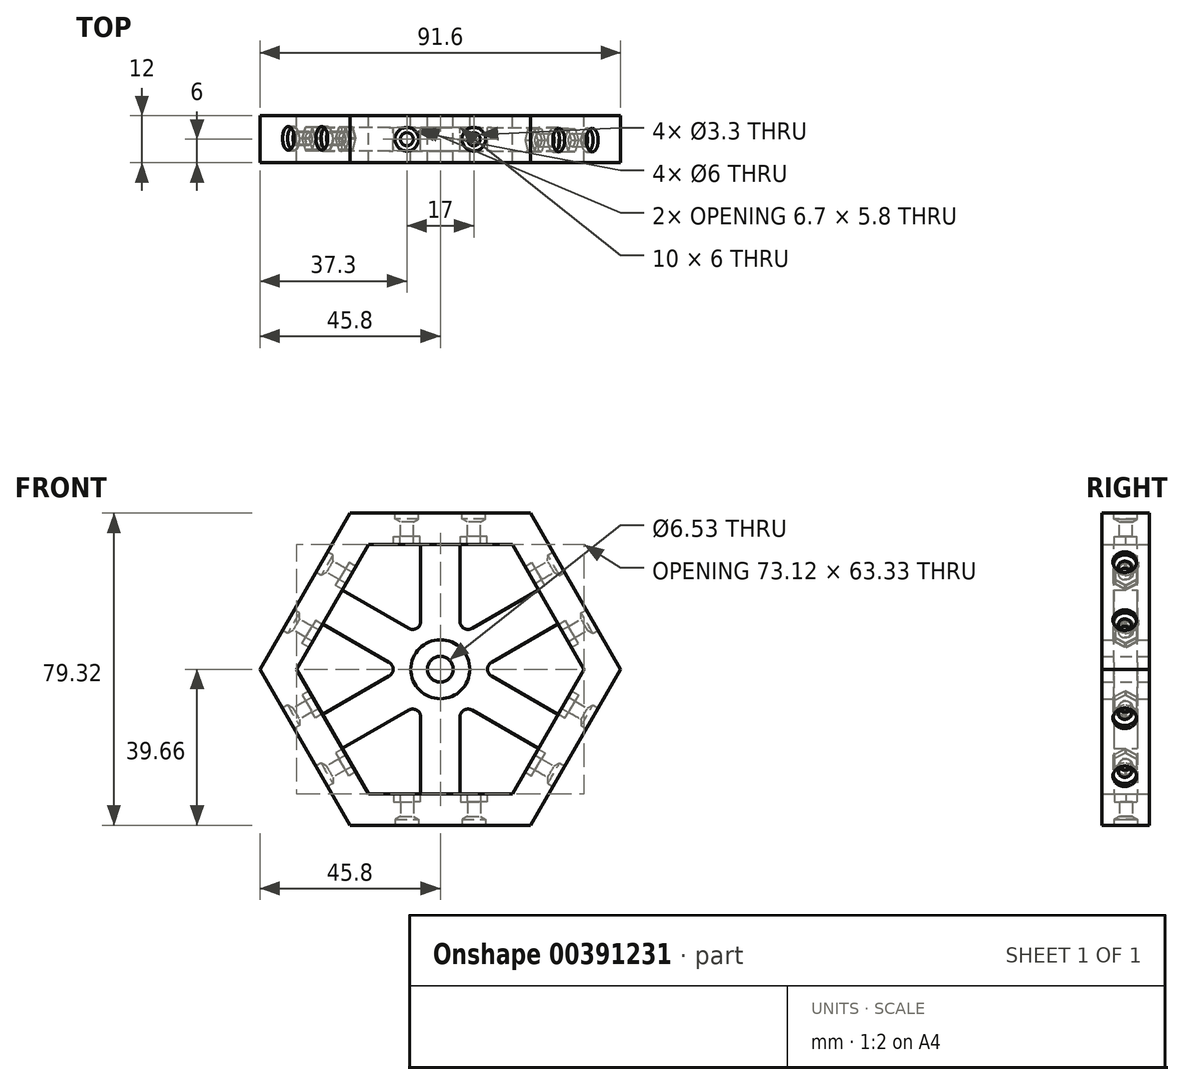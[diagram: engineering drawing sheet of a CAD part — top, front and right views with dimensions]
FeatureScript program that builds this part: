
annotation { "Feature Type Name" : "Feature", "Feature Type Description" : "" }
export const myFeature = defineFeature(function(context is Context, id is Id, definition is map)
    precondition{}
    {
        {
            var Q0;
            Q0=qCreatedBy(makeId("Front.planeOp"),FACE);
            var sketch = newSketch(context, id + "F0", { "sketchPlane" : qUnion([Q0])});
            skCircle(sketch, "E0.cCircle", {"center": v(0, 0) * mm, "radius": 39.66 * mm, "construction": true});
            skLineSegment(sketch, "E0.0", {"start": v(45.8, 0) * mm, "end": v(22.9, -39.66) * mm});
            skLineSegment(sketch, "E0.1", {"start": v(22.9, -39.66) * mm, "end": v(-22.9, -39.66) * mm});
            skLineSegment(sketch, "E0.2", {"start": v(-22.9, -39.66) * mm, "end": v(-45.8, 0) * mm});
            skLineSegment(sketch, "E0.3", {"start": v(-45.8, 0) * mm, "end": v(-22.9, 39.66) * mm});
            skLineSegment(sketch, "E0.4", {"start": v(-22.9, 39.66) * mm, "end": v(22.9, 39.66) * mm});
            skLineSegment(sketch, "E0.5", {"start": v(22.9, 39.66) * mm, "end": v(45.8, 0) * mm});
            skPoint(sketch, "E0.0.midPoint", {"position": v(34.35, -19.83) * mm});
            skCircle(sketch, "E1.cCircle", {"center": v(0, 0) * mm, "radius": 31.66 * mm, "construction": true});
            skLineSegment(sketch, "E1.0", {"start": v(36.56, 0) * mm, "end": v(18.28, -31.66) * mm});
            skLineSegment(sketch, "E1.1", {"start": v(18.28, -31.66) * mm, "end": v(-18.28, -31.66) * mm});
            skLineSegment(sketch, "E1.2", {"start": v(-18.28, -31.66) * mm, "end": v(-36.56, 0) * mm});
            skLineSegment(sketch, "E1.3", {"start": v(-36.56, 0) * mm, "end": v(-18.28, 31.66) * mm});
            skLineSegment(sketch, "E1.4", {"start": v(-18.28, 31.66) * mm, "end": v(18.28, 31.66) * mm});
            skLineSegment(sketch, "E1.5", {"start": v(18.28, 31.66) * mm, "end": v(36.56, 0) * mm});
            skPoint(sketch, "E1.0.midPoint", {"position": v(27.42, -15.83) * mm});
            skCircle(sketch, "E2", {"center": v(0, 0) * mm, "radius": 5 * mm});
            skLineSegment(sketch, "E3", {"start": v(5, -12.12) * mm, "end": v(5, -31.66) * mm});
            skLineSegment(sketch, "E4", {"start": v(-5, -12.12) * mm, "end": v(-5, -31.66) * mm});
            skLineSegment(sketch, "E5", {"start": v(-8, 10.4) * mm, "end": v(-24.92, 20.16) * mm});
            skLineSegment(sketch, "E6", {"start": v(-5, 12.12) * mm, "end": v(-5, 31.66) * mm});
            skLineSegment(sketch, "E7", {"start": v(5, 12.12) * mm, "end": v(5, 31.66) * mm});
            skLineSegment(sketch, "E8", {"start": v(-13, -1.73) * mm, "end": v(-29.92, -11.5) * mm});
            skLineSegment(sketch, "E9", {"start": v(-8, -10.4) * mm, "end": v(-24.92, -20.16) * mm});
            skLineSegment(sketch, "E10", {"start": v(8, -10.4) * mm, "end": v(24.92, -20.16) * mm});
            skLineSegment(sketch, "E11", {"start": v(13, -1.73) * mm, "end": v(29.92, -11.5) * mm});
            skLineSegment(sketch, "E12", {"start": v(13, 1.73) * mm, "end": v(29.92, 11.5) * mm});
            skLineSegment(sketch, "E13", {"start": v(8, 10.4) * mm, "end": v(24.92, 20.16) * mm});
            skLineSegment(sketch, "E14", {"start": v(-13, 1.73) * mm, "end": v(-29.92, 11.5) * mm});
            skArc(sketch, "E15.filletArc", {"start": v(13, 1.73) * mm, "mid": v(12, 0) * mm, "end": v(13, -1.73) * mm});
            skArc(sketch, "E16.filletArc", {"start": v(5, 12.12) * mm, "mid": v(6, 10.4) * mm, "end": v(8, 10.4) * mm});
            skArc(sketch, "E17.filletArc", {"start": v(-8, 10.4) * mm, "mid": v(-6, 10.4) * mm, "end": v(-5, 12.12) * mm});
            skArc(sketch, "E18.filletArc", {"start": v(-13, -1.73) * mm, "mid": v(-12, 0) * mm, "end": v(-13, 1.73) * mm});
            skPoint(sketch, "E19.newPointB", {"position": v(-5, 0) * mm});
            skArc(sketch, "E19.filletArc", {"start": v(-5, -12.12) * mm, "mid": v(-6, -10.4) * mm, "end": v(-8, -10.4) * mm});
            skPoint(sketch, "E20.newPointA", {"position": v(5, 0) * mm});
            skArc(sketch, "E20.filletArc", {"start": v(8, -10.4) * mm, "mid": v(6, -10.4) * mm, "end": v(5, -12.12) * mm});
            skCircle(sketch, "E21", {"center": v(0, 0) * mm, "radius": 7.5 * mm});
            skSolve(sketch);
        }
        {
            var Q0;
            Q0=makeQuery(id+"F0.imprint","IMPRINT",FACE,{"disambiguationData":[TD([[makeQuery(id+"F0.imprint","IMPRINT",EDGE,{"derivedFrom":sQuery(id+"F0.wireOp",EDGE,"E0.0")}),-1.0]])]});
            extrude(context, id + "F1", {"entities" : qUnion([Q0]), "depth" : 12 * mm});
        }
        {
            var Q0;
            {var subQ0=sQuery(id+"F0.wireOp",EDGE,"E6");var subQ1=sQuery(id+"F0.wireOp",EDGE,"E1.4");var subQ2=makeQuery(id+"F0.imprint","INTERSECT",VERTEX,{"derivedFrom":[subQ1,subQ0]});Q0=makeQuery(id+"F0.imprint","IMPRINT",FACE,{"disambiguationData":[TD([[makeQuery(id+"F0.imprint","IMPRINT",EDGE,{"disambiguationData":[TD([[subQ2,-1.0]])],"derivedFrom":subQ1}),-1.0]])]});}
            var Q1;
            {var subQ5=sQuery(id+"F0.wireOp",EDGE,"E3");var subQ6=sQuery(id+"F0.wireOp",EDGE,"E1.1");var subQ7=makeQuery(id+"F0.imprint","INTERSECT",VERTEX,{"derivedFrom":[subQ6,subQ5]});Q1=makeQuery(id+"F0.imprint","IMPRINT",FACE,{"disambiguationData":[TD([[makeQuery(id+"F0.imprint","IMPRINT",EDGE,{"disambiguationData":[TD([[subQ7,-1.0]])],"derivedFrom":subQ6}),-1.0]])]});}
            var Q2;
            {var subQ1=sQuery(id+"F0.wireOp",EDGE,"E1.2");var subQ5=sQuery(id+"F0.wireOp",EDGE,"E8");var subQ6=makeQuery(id+"F0.imprint","INTERSECT",VERTEX,{"derivedFrom":[subQ1,subQ5]});Q2=makeQuery(id+"F0.imprint","IMPRINT",FACE,{"disambiguationData":[TD([[makeQuery(id+"F0.imprint","IMPRINT",EDGE,{"disambiguationData":[TD([[subQ6,1.0]])],"derivedFrom":subQ1}),-1.0]])]});}
            var Q3;
            {var subQ1=sQuery(id+"F0.wireOp",EDGE,"E5");var subQ5=sQuery(id+"F0.wireOp",EDGE,"E1.3");var subQ6=makeQuery(id+"F0.imprint","INTERSECT",VERTEX,{"derivedFrom":[subQ5,subQ1]});Q3=makeQuery(id+"F0.imprint","IMPRINT",FACE,{"disambiguationData":[TD([[makeQuery(id+"F0.imprint","IMPRINT",EDGE,{"disambiguationData":[TD([[subQ6,1.0]])],"derivedFrom":subQ5}),-1.0]])]});}
            var Q4;
            {var subQ0=sQuery(id+"F0.wireOp",EDGE,"E10");var subQ1=sQuery(id+"F0.wireOp",EDGE,"E1.0");var subQ2=makeQuery(id+"F0.imprint","INTERSECT",VERTEX,{"derivedFrom":[subQ1,subQ0]});Q4=makeQuery(id+"F0.imprint","IMPRINT",FACE,{"disambiguationData":[TD([[makeQuery(id+"F0.imprint","IMPRINT",EDGE,{"disambiguationData":[TD([[subQ2,1.0]])],"derivedFrom":subQ1}),-1.0]])]});}
            var Q5;
            {var subQ0=sQuery(id+"F0.wireOp",EDGE,"E12");var subQ1=sQuery(id+"F0.wireOp",EDGE,"E1.5");var subQ2=makeQuery(id+"F0.imprint","INTERSECT",VERTEX,{"derivedFrom":[subQ1,subQ0]});Q5=makeQuery(id+"F0.imprint","IMPRINT",FACE,{"disambiguationData":[TD([[makeQuery(id+"F0.imprint","IMPRINT",EDGE,{"disambiguationData":[TD([[subQ2,1.0]])],"derivedFrom":subQ1}),-1.0]])]});}
            var Q6;
            {var subQ0=sQuery(id+"F0.wireOp",EDGE,"E7");var subQ5=sQuery(id+"F0.wireOp",EDGE,"E11");var subQ6=makeQuery(id+"F0.imprint","INTERSECT",VERTEX,{"derivedFrom":[subQ0,subQ5]});Q6=makeQuery(id+"F0.imprint","IMPRINT",FACE,{"disambiguationData":[TD([[makeQuery(id+"F0.imprint","IMPRINT",EDGE,{"disambiguationData":[TD([[subQ6,-1.0]])],"derivedFrom":subQ5}),-1.0]])]});}
            var Q7;
            {var subQ0=sQuery(id+"F0.wireOp",EDGE,"E11");var subQ5=sQuery(id+"F0.wireOp",EDGE,"E7");var subQ7=makeQuery(id+"F0.imprint","INTERSECT",VERTEX,{"derivedFrom":[subQ5,subQ0]});Q7=makeQuery(id+"F0.imprint","IMPRINT",FACE,{"disambiguationData":[TD([[makeQuery(id+"F0.imprint","IMPRINT",EDGE,{"disambiguationData":[TD([[subQ7,-1.0]])],"derivedFrom":subQ5}),1.0]])]});}
            var Q8;
            {var subQ0=sQuery(id+"F0.wireOp",EDGE,"E13");var subQ1=sQuery(id+"F0.wireOp",EDGE,"E5");var subQ2=makeQuery(id+"F0.imprint","INTERSECT",VERTEX,{"derivedFrom":[subQ1,subQ0]});Q8=makeQuery(id+"F0.imprint","IMPRINT",FACE,{"disambiguationData":[TD([[makeQuery(id+"F0.imprint","IMPRINT",EDGE,{"disambiguationData":[TD([[subQ2,-1.0]])],"derivedFrom":subQ1}),1.0]])]});}
            var Q9;
            {var subQ0=sQuery(id+"F0.wireOp",EDGE,"E6");var subQ5=sQuery(id+"F0.wireOp",EDGE,"E8");var subQ6=makeQuery(id+"F0.imprint","INTERSECT",VERTEX,{"derivedFrom":[subQ0,subQ5]});Q9=makeQuery(id+"F0.imprint","IMPRINT",FACE,{"disambiguationData":[TD([[makeQuery(id+"F0.imprint","IMPRINT",EDGE,{"disambiguationData":[TD([[subQ6,-1.0]])],"derivedFrom":subQ5}),1.0]])]});}
            var Q10;
            {var subQ0=sQuery(id+"F0.wireOp",EDGE,"E14");var subQ1=sQuery(id+"F0.wireOp",EDGE,"E4");var subQ2=makeQuery(id+"F0.imprint","INTERSECT",VERTEX,{"derivedFrom":[subQ1,subQ0]});Q10=makeQuery(id+"F0.imprint","IMPRINT",FACE,{"disambiguationData":[TD([[makeQuery(id+"F0.imprint","IMPRINT",EDGE,{"disambiguationData":[TD([[subQ2,-1.0]])],"derivedFrom":subQ1}),1.0]])]});}
            var Q11;
            {var subQ0=sQuery(id+"F0.wireOp",EDGE,"E12");var subQ1=sQuery(id+"F0.wireOp",EDGE,"E3");var subQ2=makeQuery(id+"F0.imprint","INTERSECT",VERTEX,{"derivedFrom":[subQ1,subQ0]});Q11=makeQuery(id+"F0.imprint","IMPRINT",FACE,{"disambiguationData":[TD([[makeQuery(id+"F0.imprint","IMPRINT",EDGE,{"disambiguationData":[TD([[subQ2,-1.0]])],"derivedFrom":subQ1}),-1.0]])]});}
            var Q12;
            {var subQ0=sQuery(id+"F0.wireOp",EDGE,"E5");var subQ3=sQuery(id+"F0.wireOp",EDGE,"E13");var subQ5=makeQuery(id+"F0.imprint","INTERSECT",VERTEX,{"derivedFrom":[subQ0,subQ3]});Q12=makeQuery(id+"F0.imprint","IMPRINT",FACE,{"disambiguationData":[TD([[makeQuery(id+"F0.imprint","IMPRINT",EDGE,{"disambiguationData":[TD([[subQ5,1.0]])],"derivedFrom":subQ0}),1.0]])]});}
            var Q13;
            {var subQ0=sQuery(id+"F0.wireOp",EDGE,"E6");var subQ3=sQuery(id+"F0.wireOp",EDGE,"E8");var subQ5=makeQuery(id+"F0.imprint","INTERSECT",VERTEX,{"derivedFrom":[subQ0,subQ3]});Q13=makeQuery(id+"F0.imprint","IMPRINT",FACE,{"disambiguationData":[TD([[makeQuery(id+"F0.imprint","IMPRINT",EDGE,{"disambiguationData":[TD([[subQ5,1.0]])],"derivedFrom":subQ0}),-1.0]])]});}
            var Q14;
            {var subQ0=sQuery(id+"F0.wireOp",EDGE,"E4");var subQ3=sQuery(id+"F0.wireOp",EDGE,"E14");var subQ5=makeQuery(id+"F0.imprint","INTERSECT",VERTEX,{"derivedFrom":[subQ0,subQ3]});Q14=makeQuery(id+"F0.imprint","IMPRINT",FACE,{"disambiguationData":[TD([[makeQuery(id+"F0.imprint","IMPRINT",EDGE,{"disambiguationData":[TD([[subQ5,1.0]])],"derivedFrom":subQ0}),1.0]])]});}
            var Q15;
            {var subQ0=sQuery(id+"F0.wireOp",EDGE,"E9");var subQ3=sQuery(id+"F0.wireOp",EDGE,"E10");var subQ5=makeQuery(id+"F0.imprint","INTERSECT",VERTEX,{"derivedFrom":[subQ0,subQ3]});Q15=makeQuery(id+"F0.imprint","IMPRINT",FACE,{"disambiguationData":[TD([[makeQuery(id+"F0.imprint","IMPRINT",EDGE,{"disambiguationData":[TD([[subQ5,1.0]])],"derivedFrom":subQ0}),-1.0]])]});}
            var Q16;
            {var subQ0=sQuery(id+"F0.wireOp",EDGE,"E3");var subQ3=sQuery(id+"F0.wireOp",EDGE,"E12");var subQ5=makeQuery(id+"F0.imprint","INTERSECT",VERTEX,{"derivedFrom":[subQ0,subQ3]});Q16=makeQuery(id+"F0.imprint","IMPRINT",FACE,{"disambiguationData":[TD([[makeQuery(id+"F0.imprint","IMPRINT",EDGE,{"disambiguationData":[TD([[subQ5,1.0]])],"derivedFrom":subQ0}),-1.0]])]});}
            var Q17;
            {var subQ0=sQuery(id+"F0.wireOp",EDGE,"E7");var subQ3=sQuery(id+"F0.wireOp",EDGE,"E11");var subQ5=makeQuery(id+"F0.imprint","INTERSECT",VERTEX,{"derivedFrom":[subQ0,subQ3]});Q17=makeQuery(id+"F0.imprint","IMPRINT",FACE,{"disambiguationData":[TD([[makeQuery(id+"F0.imprint","IMPRINT",EDGE,{"disambiguationData":[TD([[subQ5,1.0]])],"derivedFrom":subQ0}),1.0]])]});}
            var Q18;
            Q18=makeQuery(id+"F0.imprint","IMPRINT",FACE,{"disambiguationData":[TD([[makeQuery(id+"F0.imprint","IMPRINT",EDGE,{"derivedFrom":sQuery(id+"F0.wireOp",EDGE,"E2")}),1.0]])]});
            var Q19;
            Q19=makeQuery(id+"F0.imprint","IMPRINT",FACE,{"disambiguationData":[TD([[makeQuery(id+"F0.imprint","IMPRINT",EDGE,{"derivedFrom":sQuery(id+"F0.wireOp",EDGE,"E2")}),-1.0]])]});
            extrude(context, id + "F2", {"entities" : qUnion([Q0, Q1, Q2, Q3, Q4, Q5, Q6, Q7, Q8, Q9, Q10, Q11, Q12, Q13, Q14, Q15, Q16, Q17, Q18, Q19]), "operationType" : NewBodyOperationType.ADD, "depth" : 9 * mm, "hasSecondDirection" : true, "secondDirectionOppositeDirection" : false, "secondDirectionDepth" : 3 * mm});
        }
        {
            var Q0;
            Q0=makeQuery(id+"F1.opExtrude","SWEPT_FACE",FACE,{"disambiguationData":[OSD([sQuery(id+"F0.wireOp",EDGE,"E0.2")])]});
            var sketch = newSketch(context, id + "F3", { "sketchPlane" : qUnion([Q0])});
            skPoint(sketch, "E22", {"position": v(6, -8.5) * mm});
            skPoint(sketch, "E22.positionSnap0", {"position": v(6, -22.9) * mm});
            skPoint(sketch, "E23", {"position": v(6, 8.5) * mm});
            skCircle(sketch, "E24.cCircle", {"center": v(6, -8.5) * mm, "radius": 2.9 * mm, "construction": true});
            skLineSegment(sketch, "E24.0", {"start": v(6, -5.15) * mm, "end": v(8.9, -6.83) * mm});
            skLineSegment(sketch, "E24.1", {"start": v(8.9, -6.83) * mm, "end": v(8.9, -10.17) * mm});
            skLineSegment(sketch, "E24.2", {"start": v(8.9, -10.17) * mm, "end": v(6, -11.85) * mm});
            skLineSegment(sketch, "E24.3", {"start": v(6, -11.85) * mm, "end": v(3.1, -10.17) * mm});
            skLineSegment(sketch, "E24.4", {"start": v(3.1, -10.17) * mm, "end": v(3.1, -6.83) * mm});
            skLineSegment(sketch, "E24.5", {"start": v(3.1, -6.83) * mm, "end": v(6, -5.15) * mm});
            skPoint(sketch, "E24.0.midPoint", {"position": v(7.45, -5.99) * mm});
            skCircle(sketch, "E25.cCircle", {"center": v(6, 8.5) * mm, "radius": 2.9 * mm, "construction": true});
            skLineSegment(sketch, "E25.0", {"start": v(8.9, 10.17) * mm, "end": v(8.9, 6.83) * mm});
            skLineSegment(sketch, "E25.1", {"start": v(8.9, 6.83) * mm, "end": v(6, 5.15) * mm});
            skLineSegment(sketch, "E25.2", {"start": v(6, 5.15) * mm, "end": v(3.1, 6.83) * mm});
            skLineSegment(sketch, "E25.3", {"start": v(3.1, 6.83) * mm, "end": v(3.1, 10.17) * mm});
            skLineSegment(sketch, "E25.4", {"start": v(3.1, 10.17) * mm, "end": v(6, 11.85) * mm});
            skLineSegment(sketch, "E25.5", {"start": v(6, 11.85) * mm, "end": v(8.9, 10.17) * mm});
            skPoint(sketch, "E25.0.midPoint", {"position": v(8.9, 8.5) * mm});
            skSolve(sketch);
        }
        {
            var Q0;
            Q0=qSketchRegion(id+"F3",true);
            extrude(context, id + "F4", {"entities" : qUnion([Q0]), "operationType" : NewBodyOperationType.REMOVE, "oppositeDirection" : true, "depth" : 9 * mm, "hasSecondDirection" : true, "secondDirectionOppositeDirection" : true, "secondDirectionDepth" : 6 * mm});
        }
        {
            var Q0;
            Q0=sQuery(id+"F3.wireOp",VERTEX,"E22");
            var Q1;
            Q1=sQuery(id+"F3.wireOp",VERTEX,"E23");
            var Q2;
            Q2=makeQuery(id+"F1.opExtrude","SWEPT_BODY",BODY,{"disambiguationData":[OSD([sQuery(id+"F0.wireOp",EDGE,"E0.0"),sQuery(id+"F0.wireOp",EDGE,"E0.1"),sQuery(id+"F0.wireOp",EDGE,"E0.2"),sQuery(id+"F0.wireOp",EDGE,"E0.3"),sQuery(id+"F0.wireOp",EDGE,"E0.4"),sQuery(id+"F0.wireOp",EDGE,"E0.5"),sQuery(id+"F0.wireOp",EDGE,"E1.0"),sQuery(id+"F0.wireOp",EDGE,"E1.1"),sQuery(id+"F0.wireOp",EDGE,"E1.2"),sQuery(id+"F0.wireOp",EDGE,"E1.3"),sQuery(id+"F0.wireOp",EDGE,"E1.4"),sQuery(id+"F0.wireOp",EDGE,"E1.5")])]});
            hole(context, id + "F5", {"style" : HoleStyle.SIMPLE, "endStyle" : HoleEndStyle.BLIND, "standardTappedOrClearance" : lookupTablePath({ "standard" : "ISO", "fit" : "Normal", "size" : "M3", "type" : "Clearance" }), "standardBlindInLast" : lookupTablePath({ "fit" : "Standard", "standard" : "ISO", "size" : "M3", "type" : "Clearance" }), "holeDiameter" : 3.3 * mm, "holeDepth" : 13.5 * mm, "tappedDepth" : 12 * mm, "tapClearance" : 3, "locations" : qUnion([Q0, Q1]), "scope" : qUnion([Q2])});
        }
        {
            var Q0;
            Q0=sQuery(id+"F3.wireOp",VERTEX,"E22");
            var Q1;
            Q1=sQuery(id+"F3.wireOp",VERTEX,"E23");
            var Q2;
            Q2=makeQuery(id+"F1.opExtrude","SWEPT_BODY",BODY,{"disambiguationData":[OSD([sQuery(id+"F0.wireOp",EDGE,"E0.0"),sQuery(id+"F0.wireOp",EDGE,"E0.1"),sQuery(id+"F0.wireOp",EDGE,"E0.2"),sQuery(id+"F0.wireOp",EDGE,"E0.3"),sQuery(id+"F0.wireOp",EDGE,"E0.4"),sQuery(id+"F0.wireOp",EDGE,"E0.5"),sQuery(id+"F0.wireOp",EDGE,"E1.0"),sQuery(id+"F0.wireOp",EDGE,"E1.1"),sQuery(id+"F0.wireOp",EDGE,"E1.2"),sQuery(id+"F0.wireOp",EDGE,"E1.3"),sQuery(id+"F0.wireOp",EDGE,"E1.4"),sQuery(id+"F0.wireOp",EDGE,"E1.5")])]});
            hole(context, id + "F6", {"style" : HoleStyle.SIMPLE, "endStyle" : HoleEndStyle.BLIND, "holeDiameter" : 6 * mm, "holeDepth" : 1.5 * mm, "tappedDepth" : 12 * mm, "tapClearance" : 3, "locations" : qUnion([Q0, Q1]), "scope" : qUnion([Q2])});
        }
        {
            var Q0;
            Q0=makeQuery(id+"F0.imprint","IMPRINT",FACE,{"disambiguationData":[TD([[makeQuery(id+"F0.imprint","IMPRINT",EDGE,{"derivedFrom":sQuery(id+"F0.wireOp",EDGE,"E2")}),-1.0]])]});
            var Q1;
            Q1=makeQuery(id+"F0.imprint","IMPRINT",FACE,{"disambiguationData":[TD([[makeQuery(id+"F0.imprint","IMPRINT",EDGE,{"derivedFrom":sQuery(id+"F0.wireOp",EDGE,"E2")}),1.0]])]});
            extrude(context, id + "F7", {"entities" : qUnion([Q0, Q1]), "operationType" : NewBodyOperationType.ADD, "depth" : 12 * mm});
        }
        {
            var Q0;
            Q0=sQuery(id+"F0.wireOp",VERTEX,"E21.center");
            var Q1;
            Q1=makeQuery(id+"F1.opExtrude","SWEPT_BODY",BODY,{"disambiguationData":[OSD([sQuery(id+"F0.wireOp",EDGE,"E0.0"),sQuery(id+"F0.wireOp",EDGE,"E0.1"),sQuery(id+"F0.wireOp",EDGE,"E0.2"),sQuery(id+"F0.wireOp",EDGE,"E0.3"),sQuery(id+"F0.wireOp",EDGE,"E0.4"),sQuery(id+"F0.wireOp",EDGE,"E0.5"),sQuery(id+"F0.wireOp",EDGE,"E1.0"),sQuery(id+"F0.wireOp",EDGE,"E1.1"),sQuery(id+"F0.wireOp",EDGE,"E1.2"),sQuery(id+"F0.wireOp",EDGE,"E1.3"),sQuery(id+"F0.wireOp",EDGE,"E1.4"),sQuery(id+"F0.wireOp",EDGE,"E1.5")])]});
            hole(context, id + "F8", {"style" : HoleStyle.SIMPLE, "endStyle" : HoleEndStyle.BLIND, "oppositeDirection" : true, "standardTappedOrClearance" : lookupTablePath({ "standard" : "ANSI", "fit" : "Close", "size" : "1/4", "type" : "Clearance" }), "standardBlindInLast" : lookupTablePath({ "fit" : "Close", "standard" : "ANSI", "size" : "1/4", "type" : "Clearance" }), "holeDiameter" : 6.53 * mm, "holeDepth" : 15.8 * mm, "tappedDepth" : 12 * mm, "tapClearance" : 3, "locations" : qUnion([Q0]), "scope" : qUnion([Q1])});
        }
        {
            var Q0;
            Q0=makeQuery(id+"F1.opExtrude","SWEPT_FACE",FACE,{"disambiguationData":[OSD([sQuery(id+"F0.wireOp",EDGE,"E0.3")])]});
            var sketch = newSketch(context, id + "F9", { "sketchPlane" : qUnion([Q0])});
            skPoint(sketch, "E26", {"position": v(5.77, -8.5) * mm});
            skPoint(sketch, "E26.positionSnap0", {"position": v(5.77, -22.9) * mm});
            skPoint(sketch, "E27", {"position": v(5.77, 8.5) * mm});
            skCircle(sketch, "E28.cCircle", {"center": v(5.77, -8.5) * mm, "radius": 2.9 * mm, "construction": true});
            skLineSegment(sketch, "E28.0", {"start": v(5.77, -5.15) * mm, "end": v(8.67, -6.83) * mm});
            skLineSegment(sketch, "E28.1", {"start": v(8.67, -6.83) * mm, "end": v(8.67, -10.17) * mm});
            skLineSegment(sketch, "E28.2", {"start": v(8.67, -10.17) * mm, "end": v(5.77, -11.85) * mm});
            skLineSegment(sketch, "E28.3", {"start": v(5.77, -11.85) * mm, "end": v(2.87, -10.17) * mm});
            skLineSegment(sketch, "E28.4", {"start": v(2.87, -10.17) * mm, "end": v(2.87, -6.83) * mm});
            skLineSegment(sketch, "E28.5", {"start": v(2.87, -6.83) * mm, "end": v(5.77, -5.15) * mm});
            skPoint(sketch, "E28.0.midPoint", {"position": v(7.22, -5.99) * mm});
            skCircle(sketch, "E29.cCircle", {"center": v(5.77, 8.5) * mm, "radius": 2.9 * mm, "construction": true});
            skLineSegment(sketch, "E29.0", {"start": v(8.67, 10.17) * mm, "end": v(8.67, 6.83) * mm});
            skLineSegment(sketch, "E29.1", {"start": v(8.67, 6.83) * mm, "end": v(5.77, 5.15) * mm});
            skLineSegment(sketch, "E29.2", {"start": v(5.77, 5.15) * mm, "end": v(2.87, 6.83) * mm});
            skLineSegment(sketch, "E29.3", {"start": v(2.87, 6.83) * mm, "end": v(2.87, 10.17) * mm});
            skLineSegment(sketch, "E29.4", {"start": v(2.87, 10.17) * mm, "end": v(5.77, 11.85) * mm});
            skLineSegment(sketch, "E29.5", {"start": v(5.77, 11.85) * mm, "end": v(8.67, 10.17) * mm});
            skPoint(sketch, "E29.0.midPoint", {"position": v(8.67, 8.5) * mm});
            skSolve(sketch);
        }
        {
            var Q0;
            Q0 = qSketchRegion(id + "F9", true);
            extrude(context, id + "F10", {"entities" : qUnion([Q0]), "operationType" : NewBodyOperationType.REMOVE, "oppositeDirection" : true, "depth" : 9 * mm, "hasSecondDirection" : true, "secondDirectionOppositeDirection" : true, "secondDirectionDepth" : 6 * mm});
        }
        {
            var Q0;
            Q0=sQuery(id+"F9.wireOp",VERTEX,"E27");
            var Q1;
            Q1=sQuery(id+"F9.wireOp",VERTEX,"E26");
            var Q2;
            Q2=makeQuery(id+"F1.opExtrude","SWEPT_BODY",BODY,{"disambiguationData":[OSD([sQuery(id+"F0.wireOp",EDGE,"E0.0"),sQuery(id+"F0.wireOp",EDGE,"E0.1"),sQuery(id+"F0.wireOp",EDGE,"E0.2"),sQuery(id+"F0.wireOp",EDGE,"E0.3"),sQuery(id+"F0.wireOp",EDGE,"E0.4"),sQuery(id+"F0.wireOp",EDGE,"E0.5"),sQuery(id+"F0.wireOp",EDGE,"E1.0"),sQuery(id+"F0.wireOp",EDGE,"E1.1"),sQuery(id+"F0.wireOp",EDGE,"E1.2"),sQuery(id+"F0.wireOp",EDGE,"E1.3"),sQuery(id+"F0.wireOp",EDGE,"E1.4"),sQuery(id+"F0.wireOp",EDGE,"E1.5")])]});
            hole(context, id + "F11", {"style" : HoleStyle.SIMPLE, "endStyle" : HoleEndStyle.BLIND, "holeDiameter" : 6 * mm, "holeDepth" : 1.5 * mm, "tappedDepth" : 12 * mm, "tapClearance" : 3, "locations" : qUnion([Q0, Q1]), "scope" : qUnion([Q2])});
        }
        {
            var Q0;
            Q0=sQuery(id+"F9.wireOp",VERTEX,"E27");
            var Q1;
            Q1=sQuery(id+"F9.wireOp",VERTEX,"E26");
            var Q2;
            Q2=makeQuery(id+"F1.opExtrude","SWEPT_BODY",BODY,{"disambiguationData":[OSD([sQuery(id+"F0.wireOp",EDGE,"E0.0"),sQuery(id+"F0.wireOp",EDGE,"E0.1"),sQuery(id+"F0.wireOp",EDGE,"E0.2"),sQuery(id+"F0.wireOp",EDGE,"E0.3"),sQuery(id+"F0.wireOp",EDGE,"E0.4"),sQuery(id+"F0.wireOp",EDGE,"E0.5"),sQuery(id+"F0.wireOp",EDGE,"E1.0"),sQuery(id+"F0.wireOp",EDGE,"E1.1"),sQuery(id+"F0.wireOp",EDGE,"E1.2"),sQuery(id+"F0.wireOp",EDGE,"E1.3"),sQuery(id+"F0.wireOp",EDGE,"E1.4"),sQuery(id+"F0.wireOp",EDGE,"E1.5")])]});
            hole(context, id + "F12", {"style" : HoleStyle.SIMPLE, "endStyle" : HoleEndStyle.BLIND, "standardTappedOrClearance" : lookupTablePath({ "standard" : "ISO", "fit" : "Normal", "size" : "M3", "type" : "Clearance" }), "standardBlindInLast" : lookupTablePath({ "fit" : "Standard", "standard" : "ISO", "size" : "M3", "type" : "Clearance" }), "holeDiameter" : 3.3 * mm, "holeDepth" : 8 * mm, "tappedDepth" : 12 * mm, "tapClearance" : 3, "locations" : qUnion([Q0, Q1]), "scope" : qUnion([Q2])});
        }
        {
            var Q0;
            Q0=makeQuery(id+"F1.opExtrude","SWEPT_FACE",FACE,{"disambiguationData":[OSD([sQuery(id+"F0.wireOp",EDGE,"E0.4")])]});
            var sketch = newSketch(context, id + "F13", { "sketchPlane" : qUnion([Q0])});
            skPoint(sketch, "E30", {"position": v(-8.5, -6) * mm});
            skPoint(sketch, "E31", {"position": v(8.5, -6) * mm});
            skCircle(sketch, "E32.cCircle", {"center": v(8.5, -6) * mm, "radius": 2.9 * mm, "construction": true});
            skLineSegment(sketch, "E32.0", {"start": v(5.15, -6) * mm, "end": v(6.83, -3.1) * mm});
            skLineSegment(sketch, "E32.1", {"start": v(6.83, -3.1) * mm, "end": v(10.17, -3.1) * mm});
            skLineSegment(sketch, "E32.2", {"start": v(10.17, -3.1) * mm, "end": v(11.85, -6) * mm});
            skLineSegment(sketch, "E32.3", {"start": v(11.85, -6) * mm, "end": v(10.17, -8.9) * mm});
            skLineSegment(sketch, "E32.4", {"start": v(10.17, -8.9) * mm, "end": v(6.83, -8.9) * mm});
            skLineSegment(sketch, "E32.5", {"start": v(6.83, -8.9) * mm, "end": v(5.15, -6) * mm});
            skPoint(sketch, "E32.0.midPoint", {"position": v(5.99, -4.55) * mm});
            skCircle(sketch, "E33.cCircle", {"center": v(-8.5, -6) * mm, "radius": 2.9 * mm, "construction": true});
            skLineSegment(sketch, "E33.0", {"start": v(-11.85, -6) * mm, "end": v(-10.17, -3.1) * mm});
            skLineSegment(sketch, "E33.1", {"start": v(-10.17, -3.1) * mm, "end": v(-6.83, -3.1) * mm});
            skLineSegment(sketch, "E33.2", {"start": v(-6.83, -3.1) * mm, "end": v(-5.15, -6) * mm});
            skLineSegment(sketch, "E33.3", {"start": v(-5.15, -6) * mm, "end": v(-6.83, -8.9) * mm});
            skLineSegment(sketch, "E33.4", {"start": v(-6.83, -8.9) * mm, "end": v(-10.17, -8.9) * mm});
            skLineSegment(sketch, "E33.5", {"start": v(-10.17, -8.9) * mm, "end": v(-11.85, -6) * mm});
            skPoint(sketch, "E33.0.midPoint", {"position": v(-11.01, -4.55) * mm});
            skSolve(sketch);
        }
        {
            var Q0;
            Q0 = qSketchRegion(id + "F13", true);
            extrude(context, id + "F14", {"entities" : qUnion([Q0]), "operationType" : NewBodyOperationType.REMOVE, "oppositeDirection" : true, "depth" : 9 * mm, "hasSecondDirection" : true, "secondDirectionOppositeDirection" : true, "secondDirectionDepth" : 6 * mm});
        }
        {
            var Q0;
            Q0=sQuery(id+"F13.wireOp",VERTEX,"E31");
            var Q1;
            Q1=sQuery(id+"F13.wireOp",VERTEX,"E30");
            var Q2;
            Q2=makeQuery(id+"F1.opExtrude","SWEPT_BODY",BODY,{"disambiguationData":[OSD([sQuery(id+"F0.wireOp",EDGE,"E0.0"),sQuery(id+"F0.wireOp",EDGE,"E0.1"),sQuery(id+"F0.wireOp",EDGE,"E0.2"),sQuery(id+"F0.wireOp",EDGE,"E0.3"),sQuery(id+"F0.wireOp",EDGE,"E0.4"),sQuery(id+"F0.wireOp",EDGE,"E0.5"),sQuery(id+"F0.wireOp",EDGE,"E1.0"),sQuery(id+"F0.wireOp",EDGE,"E1.1"),sQuery(id+"F0.wireOp",EDGE,"E1.2"),sQuery(id+"F0.wireOp",EDGE,"E1.3"),sQuery(id+"F0.wireOp",EDGE,"E1.4"),sQuery(id+"F0.wireOp",EDGE,"E1.5")])]});
            hole(context, id + "F15", {"style" : HoleStyle.SIMPLE, "endStyle" : HoleEndStyle.BLIND, "standardTappedOrClearance" : lookupTablePath({ "standard" : "ISO", "fit" : "Normal", "size" : "M3", "type" : "Clearance" }), "standardBlindInLast" : lookupTablePath({ "fit" : "Standard", "standard" : "ISO", "size" : "M3", "type" : "Clearance" }), "holeDiameter" : 3.3 * mm, "holeDepth" : 8 * mm, "tappedDepth" : 12 * mm, "tapClearance" : 3, "locations" : qUnion([Q0, Q1]), "scope" : qUnion([Q2])});
        }
        {
            var Q0;
            Q0=sQuery(id+"F13.wireOp",VERTEX,"E31");
            var Q1;
            Q1=sQuery(id+"F13.wireOp",VERTEX,"E30");
            var Q2;
            Q2=makeQuery(id+"F1.opExtrude","SWEPT_BODY",BODY,{"disambiguationData":[OSD([sQuery(id+"F0.wireOp",EDGE,"E0.0"),sQuery(id+"F0.wireOp",EDGE,"E0.1"),sQuery(id+"F0.wireOp",EDGE,"E0.2"),sQuery(id+"F0.wireOp",EDGE,"E0.3"),sQuery(id+"F0.wireOp",EDGE,"E0.4"),sQuery(id+"F0.wireOp",EDGE,"E0.5"),sQuery(id+"F0.wireOp",EDGE,"E1.0"),sQuery(id+"F0.wireOp",EDGE,"E1.1"),sQuery(id+"F0.wireOp",EDGE,"E1.2"),sQuery(id+"F0.wireOp",EDGE,"E1.3"),sQuery(id+"F0.wireOp",EDGE,"E1.4"),sQuery(id+"F0.wireOp",EDGE,"E1.5")])]});
            hole(context, id + "F16", {"style" : HoleStyle.SIMPLE, "endStyle" : HoleEndStyle.BLIND, "holeDiameter" : 6 * mm, "holeDepth" : 1.5 * mm, "tappedDepth" : 12 * mm, "tapClearance" : 3, "locations" : qUnion([Q0, Q1]), "scope" : qUnion([Q2])});
        }
        {
            var Q0;
            Q0=makeQuery(id+"F1.opExtrude","SWEPT_FACE",FACE,{"disambiguationData":[OSD([sQuery(id+"F0.wireOp",EDGE,"E0.5")])]});
            var sketch = newSketch(context, id + "F17", { "sketchPlane" : qUnion([Q0])});
            skPoint(sketch, "E34", {"position": v(-6.23, -8.5) * mm});
            skPoint(sketch, "E34.positionSnap0", {"position": v(-6.23, -22.9) * mm});
            skPoint(sketch, "E35", {"position": v(-6.23, 8.5) * mm});
            skCircle(sketch, "E36.cCircle", {"center": v(-6.23, -8.5) * mm, "radius": 2.9 * mm, "construction": true});
            skLineSegment(sketch, "E36.0", {"start": v(-6.23, -5.15) * mm, "end": v(-3.33, -6.83) * mm});
            skLineSegment(sketch, "E36.1", {"start": v(-3.33, -6.83) * mm, "end": v(-3.33, -10.17) * mm});
            skLineSegment(sketch, "E36.2", {"start": v(-3.33, -10.17) * mm, "end": v(-6.23, -11.85) * mm});
            skLineSegment(sketch, "E36.3", {"start": v(-6.23, -11.85) * mm, "end": v(-9.13, -10.17) * mm});
            skLineSegment(sketch, "E36.4", {"start": v(-9.13, -10.17) * mm, "end": v(-9.13, -6.83) * mm});
            skLineSegment(sketch, "E36.5", {"start": v(-9.13, -6.83) * mm, "end": v(-6.23, -5.15) * mm});
            skPoint(sketch, "E36.0.midPoint", {"position": v(-4.78, -5.99) * mm});
            skCircle(sketch, "E37.cCircle", {"center": v(-6.23, 8.5) * mm, "radius": 2.9 * mm, "construction": true});
            skLineSegment(sketch, "E37.0", {"start": v(-3.33, 10.17) * mm, "end": v(-3.33, 6.83) * mm});
            skLineSegment(sketch, "E37.1", {"start": v(-3.33, 6.83) * mm, "end": v(-6.23, 5.15) * mm});
            skLineSegment(sketch, "E37.2", {"start": v(-6.23, 5.15) * mm, "end": v(-9.13, 6.83) * mm});
            skLineSegment(sketch, "E37.3", {"start": v(-9.13, 6.83) * mm, "end": v(-9.13, 10.17) * mm});
            skLineSegment(sketch, "E37.4", {"start": v(-9.13, 10.17) * mm, "end": v(-6.23, 11.85) * mm});
            skLineSegment(sketch, "E37.5", {"start": v(-6.23, 11.85) * mm, "end": v(-3.33, 10.17) * mm});
            skPoint(sketch, "E37.0.midPoint", {"position": v(-3.33, 8.5) * mm});
            skSolve(sketch);
        }
        {
            var Q0;
            Q0=makeQuery(id+"F17.imprint","IMPRINT",FACE,{"disambiguationData":[TD([[makeQuery(id+"F17.imprint","IMPRINT",EDGE,{"derivedFrom":sQuery(id+"F17.wireOp",EDGE,"E37.0")}),-1.0]])]});
            var Q1;
            Q1=makeQuery(id+"F17.imprint","IMPRINT",FACE,{"disambiguationData":[TD([[makeQuery(id+"F17.imprint","IMPRINT",EDGE,{"derivedFrom":sQuery(id+"F17.wireOp",EDGE,"E36.0")}),-1.0]])]});
            extrude(context, id + "F18", {"entities" : qUnion([Q0, Q1]), "operationType" : NewBodyOperationType.REMOVE, "oppositeDirection" : true, "depth" : 9 * mm, "hasSecondDirection" : true, "secondDirectionOppositeDirection" : true, "secondDirectionDepth" : 6 * mm});
        }
        {
            var Q0;
            Q0=sQuery(id+"F17.wireOp",VERTEX,"E34");
            var Q1;
            Q1=sQuery(id+"F17.wireOp",VERTEX,"E35");
            var Q2;
            Q2=makeQuery(id+"F1.opExtrude","SWEPT_BODY",BODY,{"disambiguationData":[OSD([sQuery(id+"F0.wireOp",EDGE,"E0.0"),sQuery(id+"F0.wireOp",EDGE,"E0.1"),sQuery(id+"F0.wireOp",EDGE,"E0.2"),sQuery(id+"F0.wireOp",EDGE,"E0.3"),sQuery(id+"F0.wireOp",EDGE,"E0.4"),sQuery(id+"F0.wireOp",EDGE,"E0.5"),sQuery(id+"F0.wireOp",EDGE,"E1.0"),sQuery(id+"F0.wireOp",EDGE,"E1.1"),sQuery(id+"F0.wireOp",EDGE,"E1.2"),sQuery(id+"F0.wireOp",EDGE,"E1.3"),sQuery(id+"F0.wireOp",EDGE,"E1.4"),sQuery(id+"F0.wireOp",EDGE,"E1.5")])]});
            hole(context, id + "F19", {"style" : HoleStyle.SIMPLE, "endStyle" : HoleEndStyle.BLIND, "holeDiameter" : 6 * mm, "holeDepth" : 1.5 * mm, "tappedDepth" : 12 * mm, "tapClearance" : 3, "locations" : qUnion([Q0, Q1]), "scope" : qUnion([Q2])});
        }
        {
            var Q0;
            Q0=sQuery(id+"F17.wireOp",VERTEX,"E34");
            var Q1;
            Q1=sQuery(id+"F17.wireOp",VERTEX,"E35");
            var Q2;
            Q2=makeQuery(id+"F1.opExtrude","SWEPT_BODY",BODY,{"disambiguationData":[OSD([sQuery(id+"F0.wireOp",EDGE,"E0.0"),sQuery(id+"F0.wireOp",EDGE,"E0.1"),sQuery(id+"F0.wireOp",EDGE,"E0.2"),sQuery(id+"F0.wireOp",EDGE,"E0.3"),sQuery(id+"F0.wireOp",EDGE,"E0.4"),sQuery(id+"F0.wireOp",EDGE,"E0.5"),sQuery(id+"F0.wireOp",EDGE,"E1.0"),sQuery(id+"F0.wireOp",EDGE,"E1.1"),sQuery(id+"F0.wireOp",EDGE,"E1.2"),sQuery(id+"F0.wireOp",EDGE,"E1.3"),sQuery(id+"F0.wireOp",EDGE,"E1.4"),sQuery(id+"F0.wireOp",EDGE,"E1.5")])]});
            hole(context, id + "F20", {"style" : HoleStyle.SIMPLE, "endStyle" : HoleEndStyle.BLIND, "standardTappedOrClearance" : lookupTablePath({ "standard" : "ISO", "fit" : "Normal", "size" : "M3", "type" : "Clearance" }), "standardBlindInLast" : lookupTablePath({ "fit" : "Standard", "standard" : "ISO", "size" : "M3", "type" : "Clearance" }), "holeDiameter" : 3.3 * mm, "holeDepth" : 8 * mm, "tappedDepth" : 12 * mm, "tapClearance" : 3, "locations" : qUnion([Q0, Q1]), "scope" : qUnion([Q2])});
        }
        {
            var Q0;
            Q0=makeQuery(id+"F1.opExtrude","SWEPT_FACE",FACE,{"disambiguationData":[OSD([sQuery(id+"F0.wireOp",EDGE,"E0.0")])]});
            var sketch = newSketch(context, id + "F21", { "sketchPlane" : qUnion([Q0])});
            skPoint(sketch, "E38", {"position": v(-6.23, -8.5) * mm});
            skPoint(sketch, "E38.positionSnap0", {"position": v(-6.23, -22.9) * mm});
            skPoint(sketch, "E39", {"position": v(-6.23, 8.5) * mm});
            skCircle(sketch, "E40.cCircle", {"center": v(-6.23, -8.5) * mm, "radius": 2.9 * mm, "construction": true});
            skLineSegment(sketch, "E40.0", {"start": v(-6.23, -5.15) * mm, "end": v(-3.33, -6.83) * mm});
            skLineSegment(sketch, "E40.1", {"start": v(-3.33, -6.83) * mm, "end": v(-3.33, -10.17) * mm});
            skLineSegment(sketch, "E40.2", {"start": v(-3.33, -10.17) * mm, "end": v(-6.23, -11.85) * mm});
            skLineSegment(sketch, "E40.3", {"start": v(-6.23, -11.85) * mm, "end": v(-9.13, -10.17) * mm});
            skLineSegment(sketch, "E40.4", {"start": v(-9.13, -10.17) * mm, "end": v(-9.13, -6.83) * mm});
            skLineSegment(sketch, "E40.5", {"start": v(-9.13, -6.83) * mm, "end": v(-6.23, -5.15) * mm});
            skPoint(sketch, "E40.0.midPoint", {"position": v(-4.78, -5.99) * mm});
            skCircle(sketch, "E41.cCircle", {"center": v(-6.23, 8.5) * mm, "radius": 2.9 * mm, "construction": true});
            skLineSegment(sketch, "E41.0", {"start": v(-3.33, 10.17) * mm, "end": v(-3.33, 6.83) * mm});
            skLineSegment(sketch, "E41.1", {"start": v(-3.33, 6.83) * mm, "end": v(-6.23, 5.15) * mm});
            skLineSegment(sketch, "E41.2", {"start": v(-6.23, 5.15) * mm, "end": v(-9.13, 6.83) * mm});
            skLineSegment(sketch, "E41.3", {"start": v(-9.13, 6.83) * mm, "end": v(-9.13, 10.17) * mm});
            skLineSegment(sketch, "E41.4", {"start": v(-9.13, 10.17) * mm, "end": v(-6.23, 11.85) * mm});
            skLineSegment(sketch, "E41.5", {"start": v(-6.23, 11.85) * mm, "end": v(-3.33, 10.17) * mm});
            skPoint(sketch, "E41.0.midPoint", {"position": v(-3.33, 8.5) * mm});
            skSolve(sketch);
        }
        {
            var Q0;
            Q0=makeQuery(id+"F21.imprint","IMPRINT",FACE,{"disambiguationData":[TD([[makeQuery(id+"F21.imprint","IMPRINT",EDGE,{"derivedFrom":sQuery(id+"F21.wireOp",EDGE,"E41.0")}),-1.0]])]});
            var Q1;
            Q1=makeQuery(id+"F21.imprint","IMPRINT",FACE,{"disambiguationData":[TD([[makeQuery(id+"F21.imprint","IMPRINT",EDGE,{"derivedFrom":sQuery(id+"F21.wireOp",EDGE,"E40.0")}),-1.0]])]});
            extrude(context, id + "F22", {"entities" : qUnion([Q0, Q1]), "operationType" : NewBodyOperationType.REMOVE, "oppositeDirection" : true, "depth" : 9 * mm, "hasSecondDirection" : true, "secondDirectionOppositeDirection" : true, "secondDirectionDepth" : 6 * mm});
        }
        {
            var Q0;
            Q0=sQuery(id+"F21.wireOp",VERTEX,"E38");
            var Q1;
            Q1=sQuery(id+"F21.wireOp",VERTEX,"E39");
            var Q2;
            Q2=makeQuery(id+"F1.opExtrude","SWEPT_BODY",BODY,{"disambiguationData":[OSD([sQuery(id+"F0.wireOp",EDGE,"E0.0"),sQuery(id+"F0.wireOp",EDGE,"E0.1"),sQuery(id+"F0.wireOp",EDGE,"E0.2"),sQuery(id+"F0.wireOp",EDGE,"E0.3"),sQuery(id+"F0.wireOp",EDGE,"E0.4"),sQuery(id+"F0.wireOp",EDGE,"E0.5"),sQuery(id+"F0.wireOp",EDGE,"E1.0"),sQuery(id+"F0.wireOp",EDGE,"E1.1"),sQuery(id+"F0.wireOp",EDGE,"E1.2"),sQuery(id+"F0.wireOp",EDGE,"E1.3"),sQuery(id+"F0.wireOp",EDGE,"E1.4"),sQuery(id+"F0.wireOp",EDGE,"E1.5")])]});
            hole(context, id + "F23", {"style" : HoleStyle.SIMPLE, "endStyle" : HoleEndStyle.BLIND, "standardTappedOrClearance" : lookupTablePath({ "standard" : "ISO", "fit" : "Normal", "size" : "M3", "type" : "Clearance" }), "standardBlindInLast" : lookupTablePath({ "fit" : "Standard", "standard" : "ISO", "size" : "M3", "type" : "Clearance" }), "holeDiameter" : 3.3 * mm, "holeDepth" : 8 * mm, "tappedDepth" : 12 * mm, "tapClearance" : 3, "locations" : qUnion([Q0, Q1]), "scope" : qUnion([Q2])});
        }
        {
            var Q0;
            Q0=sQuery(id+"F21.wireOp",VERTEX,"E38");
            var Q1;
            Q1=sQuery(id+"F21.wireOp",VERTEX,"E39");
            var Q2;
            Q2=makeQuery(id+"F1.opExtrude","SWEPT_BODY",BODY,{"disambiguationData":[OSD([sQuery(id+"F0.wireOp",EDGE,"E0.0"),sQuery(id+"F0.wireOp",EDGE,"E0.1"),sQuery(id+"F0.wireOp",EDGE,"E0.2"),sQuery(id+"F0.wireOp",EDGE,"E0.3"),sQuery(id+"F0.wireOp",EDGE,"E0.4"),sQuery(id+"F0.wireOp",EDGE,"E0.5"),sQuery(id+"F0.wireOp",EDGE,"E1.0"),sQuery(id+"F0.wireOp",EDGE,"E1.1"),sQuery(id+"F0.wireOp",EDGE,"E1.2"),sQuery(id+"F0.wireOp",EDGE,"E1.3"),sQuery(id+"F0.wireOp",EDGE,"E1.4"),sQuery(id+"F0.wireOp",EDGE,"E1.5")])]});
            hole(context, id + "F24", {"style" : HoleStyle.SIMPLE, "endStyle" : HoleEndStyle.BLIND, "holeDiameter" : 6 * mm, "holeDepth" : 1.5 * mm, "tappedDepth" : 12 * mm, "tapClearance" : 3, "locations" : qUnion([Q0, Q1]), "scope" : qUnion([Q2])});
        }
        {
            var Q0;
            Q0=makeQuery(id+"F1.opExtrude","SWEPT_FACE",FACE,{"disambiguationData":[OSD([sQuery(id+"F0.wireOp",EDGE,"E0.1")])]});
            var sketch = newSketch(context, id + "F25", { "sketchPlane" : qUnion([Q0])});
            skPoint(sketch, "E42", {"position": v(8.5, 6) * mm});
            skPoint(sketch, "E43", {"position": v(-8.5, 6) * mm});
            skCircle(sketch, "E44.cCircle", {"center": v(-8.5, 6) * mm, "radius": 2.9 * mm, "construction": true});
            skLineSegment(sketch, "E44.0", {"start": v(-5.15, 6) * mm, "end": v(-6.83, 3.1) * mm});
            skLineSegment(sketch, "E44.1", {"start": v(-6.83, 3.1) * mm, "end": v(-10.17, 3.1) * mm});
            skLineSegment(sketch, "E44.2", {"start": v(-10.17, 3.1) * mm, "end": v(-11.85, 6) * mm});
            skLineSegment(sketch, "E44.3", {"start": v(-11.85, 6) * mm, "end": v(-10.17, 8.9) * mm});
            skLineSegment(sketch, "E44.4", {"start": v(-10.17, 8.9) * mm, "end": v(-6.83, 8.9) * mm});
            skLineSegment(sketch, "E44.5", {"start": v(-6.83, 8.9) * mm, "end": v(-5.15, 6) * mm});
            skPoint(sketch, "E44.0.midPoint", {"position": v(-5.99, 4.55) * mm});
            skCircle(sketch, "E45.cCircle", {"center": v(8.5, 6) * mm, "radius": 2.9 * mm, "construction": true});
            skLineSegment(sketch, "E45.0", {"start": v(10.17, 3.1) * mm, "end": v(6.83, 3.1) * mm});
            skLineSegment(sketch, "E45.1", {"start": v(6.83, 3.1) * mm, "end": v(5.15, 6) * mm});
            skLineSegment(sketch, "E45.2", {"start": v(5.15, 6) * mm, "end": v(6.83, 8.9) * mm});
            skLineSegment(sketch, "E45.3", {"start": v(6.83, 8.9) * mm, "end": v(10.17, 8.9) * mm});
            skLineSegment(sketch, "E45.4", {"start": v(10.17, 8.9) * mm, "end": v(11.85, 6) * mm});
            skLineSegment(sketch, "E45.5", {"start": v(11.85, 6) * mm, "end": v(10.17, 3.1) * mm});
            skPoint(sketch, "E45.0.midPoint", {"position": v(8.5, 3.1) * mm});
            skSolve(sketch);
        }
        {
            var Q0;
            Q0 = qSketchRegion(id + "F25", true);
            extrude(context, id + "F26", {"entities" : qUnion([Q0]), "operationType" : NewBodyOperationType.REMOVE, "oppositeDirection" : true, "depth" : 9 * mm, "hasSecondDirection" : true, "secondDirectionOppositeDirection" : true, "secondDirectionDepth" : 6 * mm});
        }
        {
            var Q0;
            Q0=sQuery(id+"F25.wireOp",VERTEX,"E43");
            var Q1;
            Q1=sQuery(id+"F25.wireOp",VERTEX,"E42");
            var Q2;
            Q2=makeQuery(id+"F1.opExtrude","SWEPT_BODY",BODY,{"disambiguationData":[OSD([sQuery(id+"F0.wireOp",EDGE,"E0.0"),sQuery(id+"F0.wireOp",EDGE,"E0.1"),sQuery(id+"F0.wireOp",EDGE,"E0.2"),sQuery(id+"F0.wireOp",EDGE,"E0.3"),sQuery(id+"F0.wireOp",EDGE,"E0.4"),sQuery(id+"F0.wireOp",EDGE,"E0.5"),sQuery(id+"F0.wireOp",EDGE,"E1.0"),sQuery(id+"F0.wireOp",EDGE,"E1.1"),sQuery(id+"F0.wireOp",EDGE,"E1.2"),sQuery(id+"F0.wireOp",EDGE,"E1.3"),sQuery(id+"F0.wireOp",EDGE,"E1.4"),sQuery(id+"F0.wireOp",EDGE,"E1.5")])]});
            hole(context, id + "F27", {"style" : HoleStyle.SIMPLE, "endStyle" : HoleEndStyle.BLIND, "holeDiameter" : 6 * mm, "holeDepth" : 1.5 * mm, "tappedDepth" : 12 * mm, "tapClearance" : 3, "locations" : qUnion([Q0, Q1]), "scope" : qUnion([Q2])});
        }
        {
            var Q0;
            Q0=sQuery(id+"F25.wireOp",VERTEX,"E43");
            var Q1;
            Q1=sQuery(id+"F25.wireOp",VERTEX,"E42");
            var Q2;
            Q2=makeQuery(id+"F1.opExtrude","SWEPT_BODY",BODY,{"disambiguationData":[OSD([sQuery(id+"F0.wireOp",EDGE,"E0.0"),sQuery(id+"F0.wireOp",EDGE,"E0.1"),sQuery(id+"F0.wireOp",EDGE,"E0.2"),sQuery(id+"F0.wireOp",EDGE,"E0.3"),sQuery(id+"F0.wireOp",EDGE,"E0.4"),sQuery(id+"F0.wireOp",EDGE,"E0.5"),sQuery(id+"F0.wireOp",EDGE,"E1.0"),sQuery(id+"F0.wireOp",EDGE,"E1.1"),sQuery(id+"F0.wireOp",EDGE,"E1.2"),sQuery(id+"F0.wireOp",EDGE,"E1.3"),sQuery(id+"F0.wireOp",EDGE,"E1.4"),sQuery(id+"F0.wireOp",EDGE,"E1.5")])]});
            hole(context, id + "F28", {"style" : HoleStyle.SIMPLE, "endStyle" : HoleEndStyle.BLIND, "standardTappedOrClearance" : lookupTablePath({ "standard" : "ISO", "fit" : "Normal", "size" : "M3", "type" : "Clearance" }), "standardBlindInLast" : lookupTablePath({ "fit" : "Standard", "standard" : "ISO", "size" : "M3", "type" : "Clearance" }), "holeDiameter" : 3.3 * mm, "holeDepth" : 8 * mm, "tappedDepth" : 12 * mm, "tapClearance" : 3, "locations" : qUnion([Q0, Q1]), "scope" : qUnion([Q2])});
        }
    });
